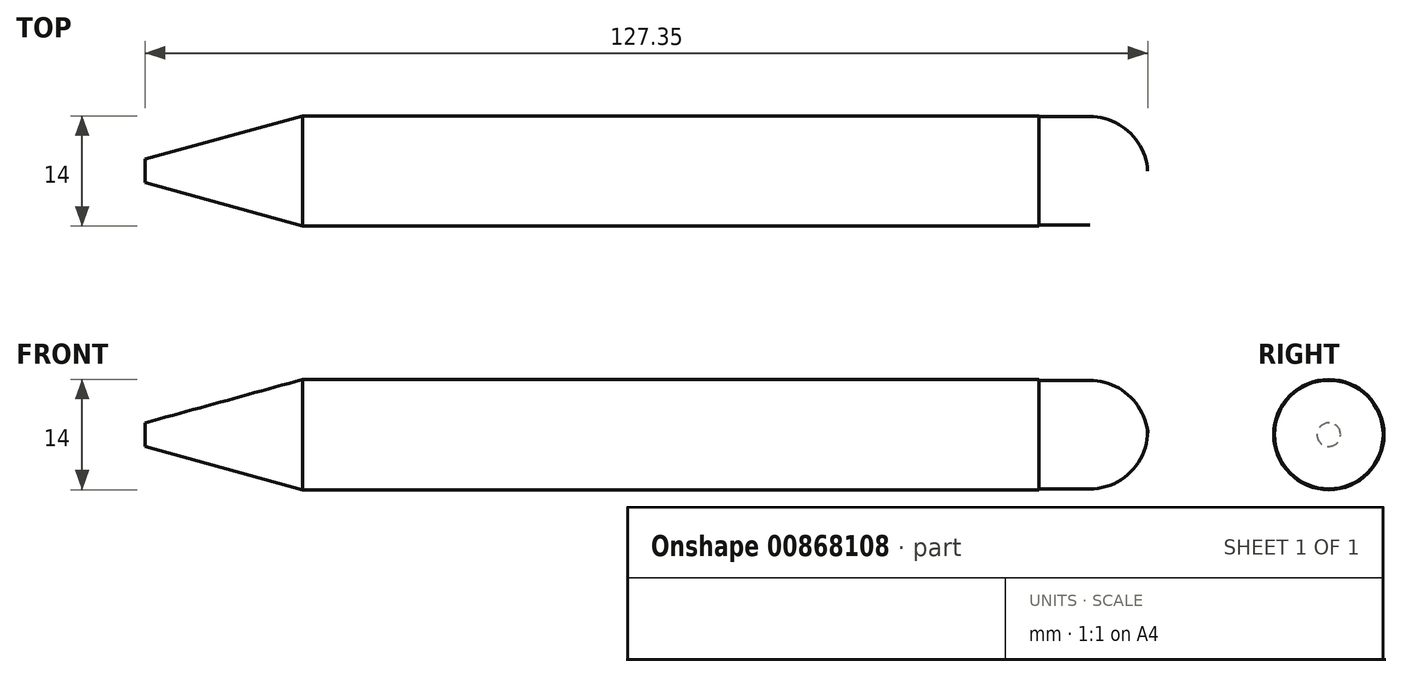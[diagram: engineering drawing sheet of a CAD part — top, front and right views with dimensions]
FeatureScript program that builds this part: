
annotation { "Feature Type Name" : "Feature", "Feature Type Description" : "" }
export const myFeature = defineFeature(function(context is Context, id is Id, definition is map)
    precondition{}
    {
        {
            var Q0;
            Q0=qCreatedBy(makeId("Top.planeOp"),FACE);
            var sketch = newSketch(context, id + "F0", { "sketchPlane" : qUnion([Q0])});
            skLineSegment(sketch, "E0", {"start": v(0, 0) * mm, "end": v(0, -1.5) * mm});
            skLineSegment(sketch, "E1", {"start": v(0, -1.5) * mm, "end": v(20, -7) * mm});
            skLineSegment(sketch, "E2", {"start": v(20, -7) * mm, "end": v(113.5, -7) * mm});
            skLineSegment(sketch, "E3", {"start": v(113.5, -7) * mm, "end": v(113.5, -7) * mm});
            skLineSegment(sketch, "E4", {"start": v(113.5, -7) * mm, "end": v(113.5, -6.9) * mm});
            skLineSegment(sketch, "E5", {"start": v(0, 0) * mm, "end": v(119.83, 0) * mm});
            skPoint(sketch, "E6.start.orphan", {"position": v(118, -2.9) * mm});
            skLineSegment(sketch, "E7", {"start": v(113.5, -6.9) * mm, "end": v(119.98, -6.9) * mm});
            skLineSegment(sketch, "E8", {"start": v(119.83, 0) * mm, "end": v(127.33, 0) * mm});
            skArc(sketch, "E9", {"start": v(119.98, -6.9) * mm, "mid": v(125.02, -4.9) * mm, "end": v(127.33, 0) * mm});
            skSolve(sketch);
        }
        {
            var Q0;
            Q0 = qSketchRegion(id + "F0", true);
            var Q1;
            Q1=sQuery(id+"F0.wireOp",EDGE,"E5");
            revolve(context, id + "F1", {"surfaceOperationType" : NewSurfaceOperationType.NEW, "entities" : qUnion([Q0]), "axis" : qUnion([Q1]), "revolveType" : RevolveType.FULL});
        }
    });
